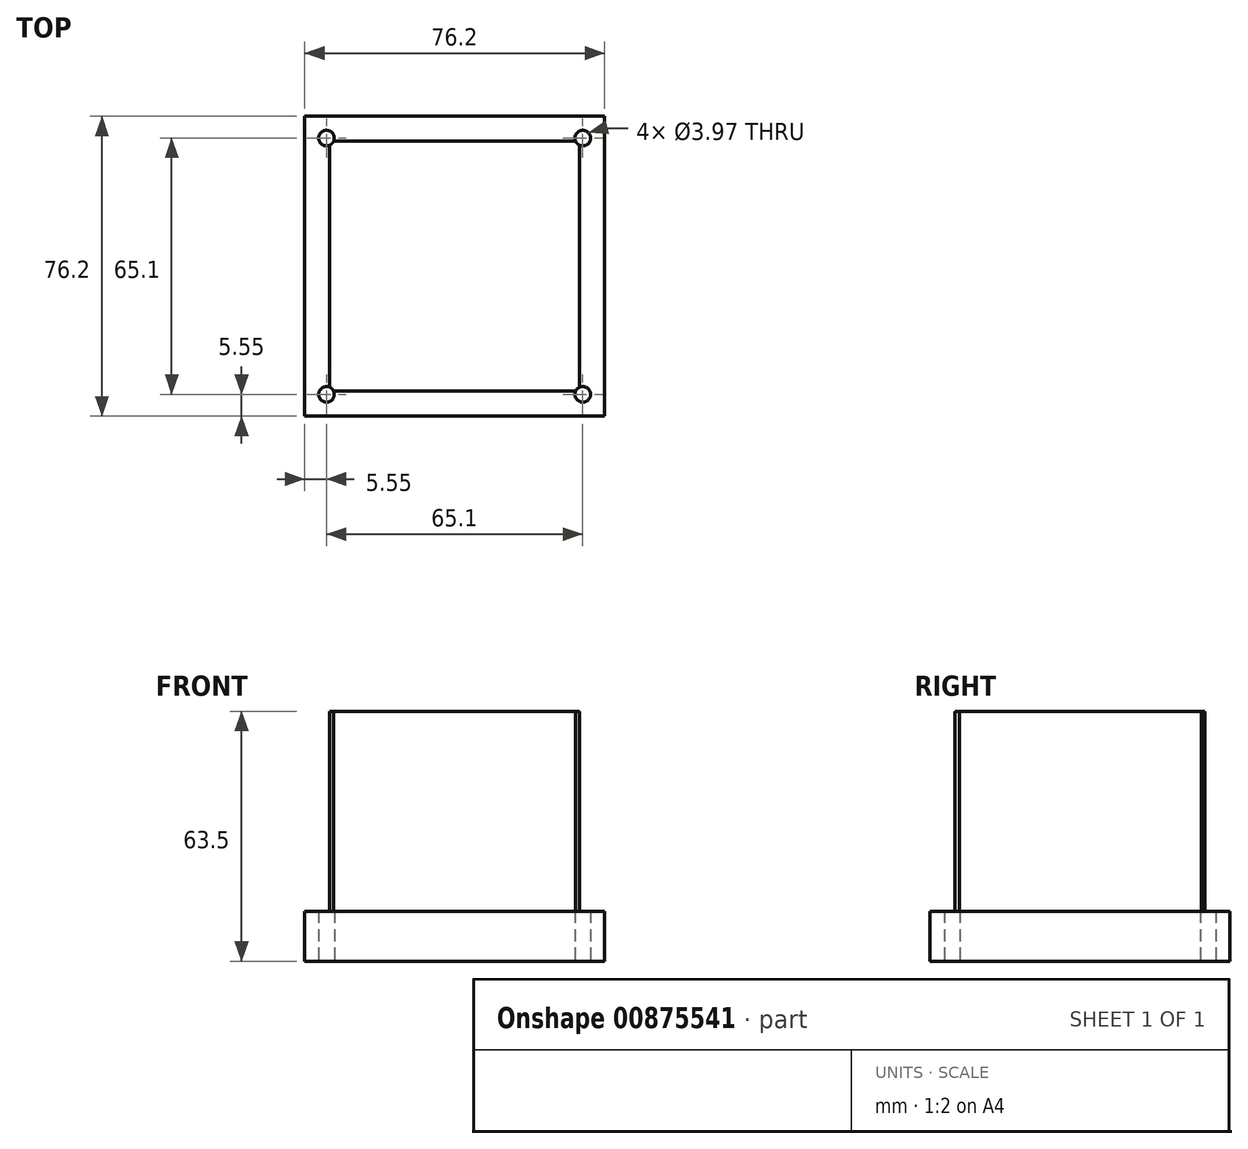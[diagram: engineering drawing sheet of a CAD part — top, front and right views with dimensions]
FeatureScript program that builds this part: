
annotation { "Feature Type Name" : "Feature", "Feature Type Description" : "" }
export const myFeature = defineFeature(function(context is Context, id is Id, definition is map)
    precondition{}
    {
        {
            var Q0;
            Q0=qCreatedBy(makeId("Top.planeOp"),FACE);
            var sketch = newSketch(context, id + "F0", { "sketchPlane" : qUnion([Q0])});
            skLineSegment(sketch, "E0.bottom", {"start": v(38.1, -38.1) * mm, "end": v(-38.1, -38.1) * mm});
            skLineSegment(sketch, "E0.top", {"start": v(38.1, 38.1) * mm, "end": v(-38.1, 38.1) * mm});
            skLineSegment(sketch, "E0.left", {"start": v(38.1, -38.1) * mm, "end": v(38.1, 38.1) * mm});
            skLineSegment(sketch, "E0.right", {"start": v(-38.1, -38.1) * mm, "end": v(-38.1, 38.1) * mm});
            skPoint(sketch, "E0.middle", {"position": v(0, 0) * mm});
            skLineSegment(sketch, "E1.bottom", {"start": v(32.55, -32.55) * mm, "end": v(-32.55, -32.55) * mm});
            skLineSegment(sketch, "E1.top", {"start": v(32.55, 32.55) * mm, "end": v(-32.55, 32.55) * mm});
            skLineSegment(sketch, "E1.left", {"start": v(32.55, -32.55) * mm, "end": v(32.55, 32.55) * mm});
            skLineSegment(sketch, "E1.right", {"start": v(-32.55, -32.55) * mm, "end": v(-32.55, 32.55) * mm});
            skCircle(sketch, "E2", {"center": v(-32.55, 32.55) * mm, "radius": 1.98 * mm});
            skCircle(sketch, "E3", {"center": v(32.55, 32.55) * mm, "radius": 1.98 * mm});
            skCircle(sketch, "E4", {"center": v(32.55, -32.55) * mm, "radius": 1.98 * mm});
            skCircle(sketch, "E5", {"center": v(-32.55, -32.55) * mm, "radius": 1.98 * mm});
            skLineSegment(sketch, "E6.bottom", {"start": v(31.75, -31.75) * mm, "end": v(-31.75, -31.75) * mm});
            skLineSegment(sketch, "E6.top", {"start": v(31.75, 31.75) * mm, "end": v(-31.75, 31.75) * mm});
            skLineSegment(sketch, "E6.left", {"start": v(31.75, -31.75) * mm, "end": v(31.75, 31.75) * mm});
            skLineSegment(sketch, "E6.right", {"start": v(-31.75, -31.75) * mm, "end": v(-31.75, 31.75) * mm});
            skSolve(sketch);
        }
        {
            var Q0;
            Q0=makeQuery(id+"F0.imprint","IMPRINT",FACE,{"disambiguationData":[TD([[makeQuery(id+"F0.imprint","IMPRINT",EDGE,{"derivedFrom":sQuery(id+"F0.wireOp",EDGE,"E0.bottom")}),-1.0]])]});
            var Q1;
            {var subQ3=sQuery(id+"F0.wireOp",EDGE,"E6.right");var subQ5=sQuery(id+"F0.wireOp",EDGE,"E2");var subQ6=makeQuery(id+"F0.imprint","INTERSECT",VERTEX,{"derivedFrom":[subQ5,subQ3]});Q1=makeQuery(id+"F0.imprint","IMPRINT",FACE,{"disambiguationData":[TD([[makeQuery(id+"F0.imprint","IMPRINT",EDGE,{"disambiguationData":[TD([[subQ6,-1.0]])],"derivedFrom":subQ5}),-1.0]])]});}
            var Q2;
            {var subQ0=sQuery(id+"F0.wireOp",EDGE,"E4");var subQ1=sQuery(id+"F0.wireOp",EDGE,"E1.left");var subQ2=makeQuery(id+"F0.imprint","INTERSECT",VERTEX,{"derivedFrom":[subQ1,subQ0]});Q2=makeQuery(id+"F0.imprint","IMPRINT",FACE,{"disambiguationData":[TD([[makeQuery(id+"F0.imprint","IMPRINT",EDGE,{"disambiguationData":[TD([[subQ2,-1.0]])],"derivedFrom":subQ1}),1.0]])]});}
            var Q3;
            {var subQ0=sQuery(id+"F0.wireOp",EDGE,"E4");var subQ1=sQuery(id+"F0.wireOp",EDGE,"E1.bottom");var subQ2=makeQuery(id+"F0.imprint","INTERSECT",VERTEX,{"derivedFrom":[subQ1,subQ0]});Q3=makeQuery(id+"F0.imprint","IMPRINT",FACE,{"disambiguationData":[TD([[makeQuery(id+"F0.imprint","IMPRINT",EDGE,{"disambiguationData":[TD([[subQ2,-1.0]])],"derivedFrom":subQ1}),-1.0]])]});}
            var Q4;
            {var subQ0=sQuery(id+"F0.wireOp",EDGE,"E3");var subQ1=sQuery(id+"F0.wireOp",EDGE,"E1.top");var subQ2=makeQuery(id+"F0.imprint","INTERSECT",VERTEX,{"derivedFrom":[subQ1,subQ0]});Q4=makeQuery(id+"F0.imprint","IMPRINT",FACE,{"disambiguationData":[TD([[makeQuery(id+"F0.imprint","IMPRINT",EDGE,{"disambiguationData":[TD([[subQ2,-1.0]])],"derivedFrom":subQ1}),1.0]])]});}
            var Q5;
            {var subQ0=sQuery(id+"F0.wireOp",EDGE,"E5");var subQ1=sQuery(id+"F0.wireOp",EDGE,"E1.right");var subQ2=makeQuery(id+"F0.imprint","INTERSECT",VERTEX,{"derivedFrom":[subQ1,subQ0]});Q5=makeQuery(id+"F0.imprint","IMPRINT",FACE,{"disambiguationData":[TD([[makeQuery(id+"F0.imprint","IMPRINT",EDGE,{"disambiguationData":[TD([[subQ2,-1.0]])],"derivedFrom":subQ1}),-1.0]])]});}
            var Q6;
            {var subQ0=sQuery(id+"F0.wireOp",EDGE,"E1.right");var subQ1=sQuery(id+"F0.wireOp",EDGE,"E1.bottom");var subQ2=makeQuery(id+"F0.imprint","INTERSECT",VERTEX,{"derivedFrom":[subQ1,subQ0]});Q6=makeQuery(id+"F0.imprint","IMPRINT",FACE,{"disambiguationData":[TD([[makeQuery(id+"F0.imprint","IMPRINT",EDGE,{"disambiguationData":[TD([[subQ2,1.0]])],"derivedFrom":subQ1}),1.0]])]});}
            var Q7;
            {var subQ0=sQuery(id+"F0.wireOp",EDGE,"E1.left");var subQ1=sQuery(id+"F0.wireOp",EDGE,"E1.top");var subQ2=makeQuery(id+"F0.imprint","INTERSECT",VERTEX,{"derivedFrom":[subQ1,subQ0]});Q7=makeQuery(id+"F0.imprint","IMPRINT",FACE,{"disambiguationData":[TD([[makeQuery(id+"F0.imprint","IMPRINT",EDGE,{"disambiguationData":[TD([[subQ2,-1.0]])],"derivedFrom":subQ1}),-1.0]])]});}
            var Q8;
            {var subQ0=sQuery(id+"F0.wireOp",EDGE,"E1.right");var subQ1=sQuery(id+"F0.wireOp",EDGE,"E1.top");var subQ2=makeQuery(id+"F0.imprint","INTERSECT",VERTEX,{"derivedFrom":[subQ1,subQ0]});Q8=makeQuery(id+"F0.imprint","IMPRINT",FACE,{"disambiguationData":[TD([[makeQuery(id+"F0.imprint","IMPRINT",EDGE,{"disambiguationData":[TD([[subQ2,1.0]])],"derivedFrom":subQ1}),-1.0]])]});}
            var Q9;
            {var subQ0=sQuery(id+"F0.wireOp",EDGE,"E1.left");var subQ1=sQuery(id+"F0.wireOp",EDGE,"E1.bottom");var subQ2=makeQuery(id+"F0.imprint","INTERSECT",VERTEX,{"derivedFrom":[subQ1,subQ0]});Q9=makeQuery(id+"F0.imprint","IMPRINT",FACE,{"disambiguationData":[TD([[makeQuery(id+"F0.imprint","IMPRINT",EDGE,{"disambiguationData":[TD([[subQ2,-1.0]])],"derivedFrom":subQ1}),1.0]])]});}
            var Q10;
            {var subQ1=sQuery(id+"F0.wireOp",EDGE,"E1.top");var subQ5=sQuery(id+"F0.wireOp",EDGE,"E1.left");var subQ9=makeQuery(id+"F0.imprint","INTERSECT",VERTEX,{"derivedFrom":[subQ1,subQ5]});Q10=makeQuery(id+"F0.imprint","IMPRINT",FACE,{"disambiguationData":[TD([[makeQuery(id+"F0.imprint","IMPRINT",EDGE,{"disambiguationData":[TD([[subQ9,-1.0]])],"derivedFrom":subQ1}),1.0]])]});}
            var Q11;
            {var subQ1=sQuery(id+"F0.wireOp",EDGE,"E1.right");var subQ7=sQuery(id+"F0.wireOp",EDGE,"E1.bottom");var subQ10=makeQuery(id+"F0.imprint","INTERSECT",VERTEX,{"derivedFrom":[subQ7,subQ1]});Q11=makeQuery(id+"F0.imprint","IMPRINT",FACE,{"disambiguationData":[TD([[makeQuery(id+"F0.imprint","IMPRINT",EDGE,{"disambiguationData":[TD([[subQ10,1.0]])],"derivedFrom":subQ7}),-1.0]])]});}
            var Q12;
            {var subQ0=sQuery(id+"F0.wireOp",EDGE,"E6.right");var subQ1=sQuery(id+"F0.wireOp",EDGE,"E2");var subQ2=makeQuery(id+"F0.imprint","INTERSECT",VERTEX,{"derivedFrom":[subQ1,subQ0]});Q12=makeQuery(id+"F0.imprint","IMPRINT",FACE,{"disambiguationData":[TD([[makeQuery(id+"F0.imprint","IMPRINT",EDGE,{"disambiguationData":[TD([[subQ2,-1.0]])],"derivedFrom":subQ1}),1.0]])]});}
            var Q13;
            {var subQ1=sQuery(id+"F0.wireOp",EDGE,"E1.bottom");var subQ5=sQuery(id+"F0.wireOp",EDGE,"E1.left");var subQ6=makeQuery(id+"F0.imprint","INTERSECT",VERTEX,{"derivedFrom":[subQ1,subQ5]});Q13=makeQuery(id+"F0.imprint","IMPRINT",FACE,{"disambiguationData":[TD([[makeQuery(id+"F0.imprint","IMPRINT",EDGE,{"disambiguationData":[TD([[subQ6,-1.0]])],"derivedFrom":subQ1}),-1.0]])]});}
            var Q14;
            {var subQ0=sQuery(id+"F0.wireOp",EDGE,"E6.top");var subQ1=sQuery(id+"F0.wireOp",EDGE,"E3");var subQ2=makeQuery(id+"F0.imprint","INTERSECT",VERTEX,{"derivedFrom":[subQ1,subQ0]});Q14=makeQuery(id+"F0.imprint","IMPRINT",FACE,{"disambiguationData":[TD([[makeQuery(id+"F0.imprint","IMPRINT",EDGE,{"disambiguationData":[TD([[subQ2,-1.0]])],"derivedFrom":subQ1}),1.0]])]});}
            var Q15;
            {var subQ0=sQuery(id+"F0.wireOp",EDGE,"E6.bottom");var subQ1=sQuery(id+"F0.wireOp",EDGE,"E5");var subQ2=makeQuery(id+"F0.imprint","INTERSECT",VERTEX,{"derivedFrom":[subQ1,subQ0]});Q15=makeQuery(id+"F0.imprint","IMPRINT",FACE,{"disambiguationData":[TD([[makeQuery(id+"F0.imprint","IMPRINT",EDGE,{"disambiguationData":[TD([[subQ2,-1.0]])],"derivedFrom":subQ1}),1.0]])]});}
            var Q16;
            {var subQ0=sQuery(id+"F0.wireOp",EDGE,"E6.left");var subQ1=sQuery(id+"F0.wireOp",EDGE,"E4");var subQ2=makeQuery(id+"F0.imprint","INTERSECT",VERTEX,{"derivedFrom":[subQ1,subQ0]});Q16=makeQuery(id+"F0.imprint","IMPRINT",FACE,{"disambiguationData":[TD([[makeQuery(id+"F0.imprint","IMPRINT",EDGE,{"disambiguationData":[TD([[subQ2,-1.0]])],"derivedFrom":subQ1}),1.0]])]});}
            var Q17;
            {var subQ1=sQuery(id+"F0.wireOp",EDGE,"E1.right");var subQ5=sQuery(id+"F0.wireOp",EDGE,"E1.top");var subQ6=makeQuery(id+"F0.imprint","INTERSECT",VERTEX,{"derivedFrom":[subQ5,subQ1]});Q17=makeQuery(id+"F0.imprint","IMPRINT",FACE,{"disambiguationData":[TD([[makeQuery(id+"F0.imprint","IMPRINT",EDGE,{"disambiguationData":[TD([[subQ6,1.0]])],"derivedFrom":subQ5}),1.0]])]});}
            extrude(context, id + "F1", {"entities" : qUnion([Q0, Q1, Q2, Q3, Q4, Q5, Q6, Q7, Q8, Q9, Q10, Q11, Q12, Q13, Q14, Q15, Q16, Q17]), "oppositeDirection" : true, "depth" : 12.7 * mm, "offsetDistance" : 25.4 * mm});
        }
        {
            var Q0;
            {var subQ3=sQuery(id+"F0.wireOp",EDGE,"E6.right");var subQ5=sQuery(id+"F0.wireOp",EDGE,"E2");var subQ6=makeQuery(id+"F0.imprint","INTERSECT",VERTEX,{"derivedFrom":[subQ5,subQ3]});Q0=makeQuery(id+"F0.imprint","IMPRINT",FACE,{"disambiguationData":[TD([[makeQuery(id+"F0.imprint","IMPRINT",EDGE,{"disambiguationData":[TD([[subQ6,-1.0]])],"derivedFrom":subQ5}),-1.0]])]});}
            extrude(context, id + "F2", {"entities" : qUnion([Q0]), "operationType" : NewBodyOperationType.ADD, "depth" : 50.8 * mm, "offsetDistance" : 25.4 * mm});
        }
        {
            var Q0;
            {var subQ0=sQuery(id+"F0.wireOp",EDGE,"E1.right");var subQ1=sQuery(id+"F0.wireOp",EDGE,"E1.bottom");var subQ2=makeQuery(id+"F0.imprint","INTERSECT",VERTEX,{"derivedFrom":[subQ1,subQ0]});Q0=makeQuery(id+"F0.imprint","IMPRINT",FACE,{"disambiguationData":[TD([[makeQuery(id+"F0.imprint","IMPRINT",EDGE,{"disambiguationData":[TD([[subQ2,1.0]])],"derivedFrom":subQ1}),1.0]])]});}
            var Q1;
            {var subQ1=sQuery(id+"F0.wireOp",EDGE,"E1.right");var subQ7=sQuery(id+"F0.wireOp",EDGE,"E1.bottom");var subQ10=makeQuery(id+"F0.imprint","INTERSECT",VERTEX,{"derivedFrom":[subQ7,subQ1]});Q1=makeQuery(id+"F0.imprint","IMPRINT",FACE,{"disambiguationData":[TD([[makeQuery(id+"F0.imprint","IMPRINT",EDGE,{"disambiguationData":[TD([[subQ10,1.0]])],"derivedFrom":subQ7}),-1.0]])]});}
            var Q2;
            {var subQ0=sQuery(id+"F0.wireOp",EDGE,"E6.bottom");var subQ1=sQuery(id+"F0.wireOp",EDGE,"E5");var subQ2=makeQuery(id+"F0.imprint","INTERSECT",VERTEX,{"derivedFrom":[subQ1,subQ0]});Q2=makeQuery(id+"F0.imprint","IMPRINT",FACE,{"disambiguationData":[TD([[makeQuery(id+"F0.imprint","IMPRINT",EDGE,{"disambiguationData":[TD([[subQ2,-1.0]])],"derivedFrom":subQ1}),1.0]])]});}
            var Q3;
            {var subQ0=sQuery(id+"F0.wireOp",EDGE,"E1.left");var subQ1=sQuery(id+"F0.wireOp",EDGE,"E1.bottom");var subQ2=makeQuery(id+"F0.imprint","INTERSECT",VERTEX,{"derivedFrom":[subQ1,subQ0]});Q3=makeQuery(id+"F0.imprint","IMPRINT",FACE,{"disambiguationData":[TD([[makeQuery(id+"F0.imprint","IMPRINT",EDGE,{"disambiguationData":[TD([[subQ2,-1.0]])],"derivedFrom":subQ1}),1.0]])]});}
            var Q4;
            {var subQ1=sQuery(id+"F0.wireOp",EDGE,"E1.bottom");var subQ5=sQuery(id+"F0.wireOp",EDGE,"E1.left");var subQ6=makeQuery(id+"F0.imprint","INTERSECT",VERTEX,{"derivedFrom":[subQ1,subQ5]});Q4=makeQuery(id+"F0.imprint","IMPRINT",FACE,{"disambiguationData":[TD([[makeQuery(id+"F0.imprint","IMPRINT",EDGE,{"disambiguationData":[TD([[subQ6,-1.0]])],"derivedFrom":subQ1}),-1.0]])]});}
            var Q5;
            {var subQ0=sQuery(id+"F0.wireOp",EDGE,"E6.left");var subQ1=sQuery(id+"F0.wireOp",EDGE,"E4");var subQ2=makeQuery(id+"F0.imprint","INTERSECT",VERTEX,{"derivedFrom":[subQ1,subQ0]});Q5=makeQuery(id+"F0.imprint","IMPRINT",FACE,{"disambiguationData":[TD([[makeQuery(id+"F0.imprint","IMPRINT",EDGE,{"disambiguationData":[TD([[subQ2,-1.0]])],"derivedFrom":subQ1}),1.0]])]});}
            var Q6;
            {var subQ0=sQuery(id+"F0.wireOp",EDGE,"E6.top");var subQ1=sQuery(id+"F0.wireOp",EDGE,"E3");var subQ2=makeQuery(id+"F0.imprint","INTERSECT",VERTEX,{"derivedFrom":[subQ1,subQ0]});Q6=makeQuery(id+"F0.imprint","IMPRINT",FACE,{"disambiguationData":[TD([[makeQuery(id+"F0.imprint","IMPRINT",EDGE,{"disambiguationData":[TD([[subQ2,-1.0]])],"derivedFrom":subQ1}),1.0]])]});}
            var Q7;
            {var subQ1=sQuery(id+"F0.wireOp",EDGE,"E1.top");var subQ5=sQuery(id+"F0.wireOp",EDGE,"E1.left");var subQ9=makeQuery(id+"F0.imprint","INTERSECT",VERTEX,{"derivedFrom":[subQ1,subQ5]});Q7=makeQuery(id+"F0.imprint","IMPRINT",FACE,{"disambiguationData":[TD([[makeQuery(id+"F0.imprint","IMPRINT",EDGE,{"disambiguationData":[TD([[subQ9,-1.0]])],"derivedFrom":subQ1}),1.0]])]});}
            var Q8;
            {var subQ0=sQuery(id+"F0.wireOp",EDGE,"E1.left");var subQ1=sQuery(id+"F0.wireOp",EDGE,"E1.top");var subQ2=makeQuery(id+"F0.imprint","INTERSECT",VERTEX,{"derivedFrom":[subQ1,subQ0]});Q8=makeQuery(id+"F0.imprint","IMPRINT",FACE,{"disambiguationData":[TD([[makeQuery(id+"F0.imprint","IMPRINT",EDGE,{"disambiguationData":[TD([[subQ2,-1.0]])],"derivedFrom":subQ1}),-1.0]])]});}
            var Q9;
            {var subQ0=sQuery(id+"F0.wireOp",EDGE,"E1.right");var subQ1=sQuery(id+"F0.wireOp",EDGE,"E1.top");var subQ2=makeQuery(id+"F0.imprint","INTERSECT",VERTEX,{"derivedFrom":[subQ1,subQ0]});Q9=makeQuery(id+"F0.imprint","IMPRINT",FACE,{"disambiguationData":[TD([[makeQuery(id+"F0.imprint","IMPRINT",EDGE,{"disambiguationData":[TD([[subQ2,1.0]])],"derivedFrom":subQ1}),-1.0]])]});}
            var Q10;
            {var subQ1=sQuery(id+"F0.wireOp",EDGE,"E1.right");var subQ5=sQuery(id+"F0.wireOp",EDGE,"E1.top");var subQ6=makeQuery(id+"F0.imprint","INTERSECT",VERTEX,{"derivedFrom":[subQ5,subQ1]});Q10=makeQuery(id+"F0.imprint","IMPRINT",FACE,{"disambiguationData":[TD([[makeQuery(id+"F0.imprint","IMPRINT",EDGE,{"disambiguationData":[TD([[subQ6,1.0]])],"derivedFrom":subQ5}),1.0]])]});}
            var Q11;
            {var subQ0=sQuery(id+"F0.wireOp",EDGE,"E6.right");var subQ1=sQuery(id+"F0.wireOp",EDGE,"E2");var subQ2=makeQuery(id+"F0.imprint","INTERSECT",VERTEX,{"derivedFrom":[subQ1,subQ0]});Q11=makeQuery(id+"F0.imprint","IMPRINT",FACE,{"disambiguationData":[TD([[makeQuery(id+"F0.imprint","IMPRINT",EDGE,{"disambiguationData":[TD([[subQ2,-1.0]])],"derivedFrom":subQ1}),1.0]])]});}
            extrude(context, id + "F3", {"entities" : qUnion([Q0, Q1, Q2, Q3, Q4, Q5, Q6, Q7, Q8, Q9, Q10, Q11]), "operationType" : NewBodyOperationType.REMOVE, "endBound" : BoundingType.UP_TO_NEXT, "oppositeDirection" : true, "depth" : 25.4 * mm, "offsetDistance" : 25.4 * mm});
        }
    });
